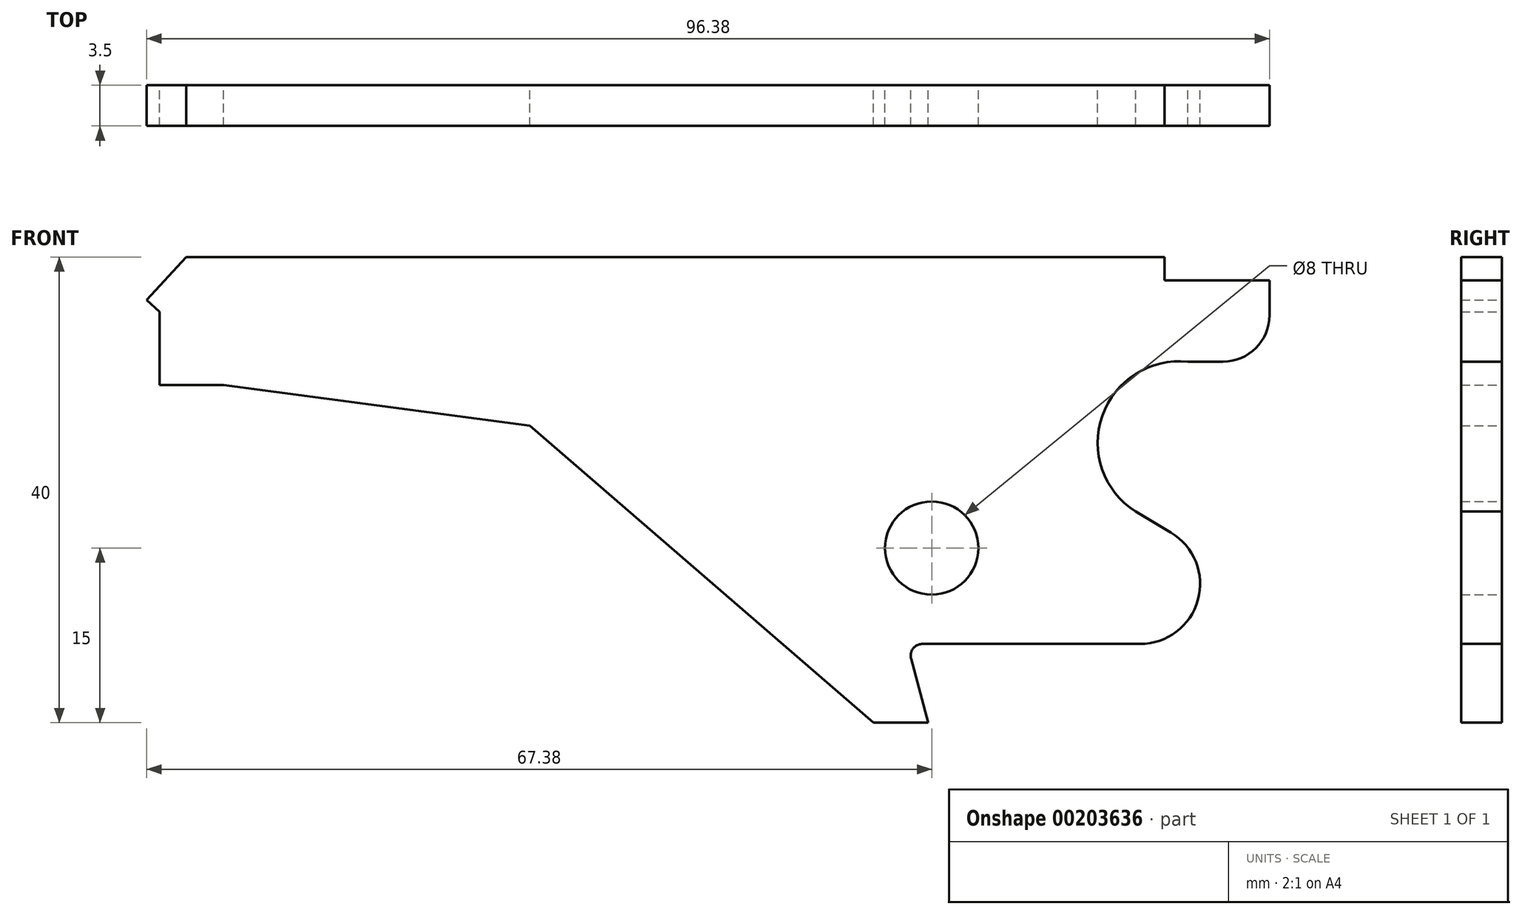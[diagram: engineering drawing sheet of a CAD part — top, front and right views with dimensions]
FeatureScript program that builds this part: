
annotation { "Feature Type Name" : "Feature", "Feature Type Description" : "" }
export const myFeature = defineFeature(function(context is Context, id is Id, definition is map)
    precondition{}
    {
        {
            var Q0;
            Q0=qCreatedBy(makeId("Front.planeOp"),FACE);
            var sketch = newSketch(context, id + "F0", { "sketchPlane" : qUnion([Q0])});
            skLineSegment(sketch, "E0", {"start": v(0, 0) * mm, "end": v(-84, 0) * mm});
            skLineSegment(sketch, "E1", {"start": v(-84, 0) * mm, "end": v(-87.38, -3.69) * mm});
            skLineSegment(sketch, "E2", {"start": v(-87.38, -3.69) * mm, "end": v(-86.27, -4.7) * mm});
            skLineSegment(sketch, "E3", {"start": v(-86.27, -4.7) * mm, "end": v(-86.27, -11) * mm});
            skLineSegment(sketch, "E4", {"start": v(-86.27, -11) * mm, "end": v(-80.77, -11) * mm});
            skLineSegment(sketch, "E5", {"start": v(-80.77, -11) * mm, "end": v(-54.5, -14.5) * mm});
            skLineSegment(sketch, "E6", {"start": v(-54.5, -14.5) * mm, "end": v(-25, -40) * mm});
            skLineSegment(sketch, "E7", {"start": v(-25, -40) * mm, "end": v(-20.3, -40) * mm});
            skLineSegment(sketch, "E8", {"start": v(-20.3, -40) * mm, "end": v(-21.77, -34.5) * mm});
            skLineSegment(sketch, "E9", {"start": v(-20.8, -33.24) * mm, "end": v(-2.11, -33.24) * mm});
            skLineSegment(sketch, "E10", {"start": v(0, 0) * mm, "end": v(0, -2) * mm});
            skLineSegment(sketch, "E11", {"start": v(0, -2) * mm, "end": v(9, -2) * mm});
            skLineSegment(sketch, "E12", {"start": v(9, -2) * mm, "end": v(9, -5) * mm});
            skLineSegment(sketch, "E13", {"start": v(5, -9) * mm, "end": v(2, -9) * mm});
            skCircle(sketch, "E14", {"center": v(-2.11, -28.09) * mm, "radius": 5.15 * mm});
            skCircle(sketch, "E15", {"center": v(1.25, -15.96) * mm, "radius": 7 * mm});
            skLineSegment(sketch, "E16", {"start": v(0.54, -23.67) * mm, "end": v(-2.5, -21.87) * mm});
            skCircle(sketch, "E17", {"center": v(-20, -25) * mm, "radius": 4 * mm});
            skPoint(sketch, "E18.visualSharp", {"position": v(-22.11, -33.24) * mm});
            skArc(sketch, "E18.filletArc", {"start": v(-20.8, -33.24) * mm, "mid": v(-21.6, -33.63) * mm, "end": v(-21.77, -34.5) * mm});
            skPoint(sketch, "E19.visualSharp", {"position": v(9, -9) * mm});
            skArc(sketch, "E19.filletArc", {"start": v(5, -9) * mm, "mid": v(7.83, -7.83) * mm, "end": v(9, -5) * mm});
            skSolve(sketch);
        }
        {
            var Q0;
            {var subQ0=sQuery(id+"F0.wireOp",EDGE,"E16");var subQ1=sQuery(id+"F0.wireOp",EDGE,"E14");var subQ2=makeQuery(id+"F0.imprint","INTERSECT",VERTEX,{"disambiguationData":[OD(0.0)],"derivedFrom":[subQ1,subQ0]});Q0=makeQuery(id+"F0.imprint","IMPRINT",FACE,{"disambiguationData":[TD([[makeQuery(id+"F0.imprint","IMPRINT",EDGE,{"disambiguationData":[TD([[subQ2,-1.0]])],"derivedFrom":subQ1}),1.0]])]});}
            var Q1;
            {var subQ0=sQuery(id+"F0.wireOp",EDGE,"E14");var subQ1=makeQuery(id+"F0.imprint","INTERSECT",VERTEX,{"derivedFrom":[sQuery(id+"F0.wireOp",EDGE,"E9"),subQ0]});Q1=makeQuery(id+"F0.imprint","IMPRINT",FACE,{"disambiguationData":[TD([[makeQuery(id+"F0.imprint","IMPRINT",EDGE,{"disambiguationData":[TD([[subQ1,1.0]])],"derivedFrom":subQ0}),1.0]])]});}
            var Q2;
            {var subQ0=sQuery(id+"F0.wireOp",EDGE,"E16");var subQ1=sQuery(id+"F0.wireOp",EDGE,"E15");var subQ2=makeQuery(id+"F0.imprint","INTERSECT",VERTEX,{"disambiguationData":[OD(0.0)],"derivedFrom":[subQ1,subQ0]});Q2=makeQuery(id+"F0.imprint","IMPRINT",FACE,{"disambiguationData":[TD([[makeQuery(id+"F0.imprint","IMPRINT",EDGE,{"disambiguationData":[TD([[subQ2,-1.0]])],"derivedFrom":subQ1}),1.0]])]});}
            var Q3;
            Q3=makeQuery(id+"F0.imprint","IMPRINT",FACE,{"disambiguationData":[TD([[makeQuery(id+"F0.imprint","IMPRINT",EDGE,{"derivedFrom":sQuery(id+"F0.wireOp",EDGE,"E0")}),1.0]])]});
            extrude(context, id + "F1", {"entities" : qUnion([Q0, Q1, Q2, Q3]), "depth" : 3.5 * mm});
        }
    });
